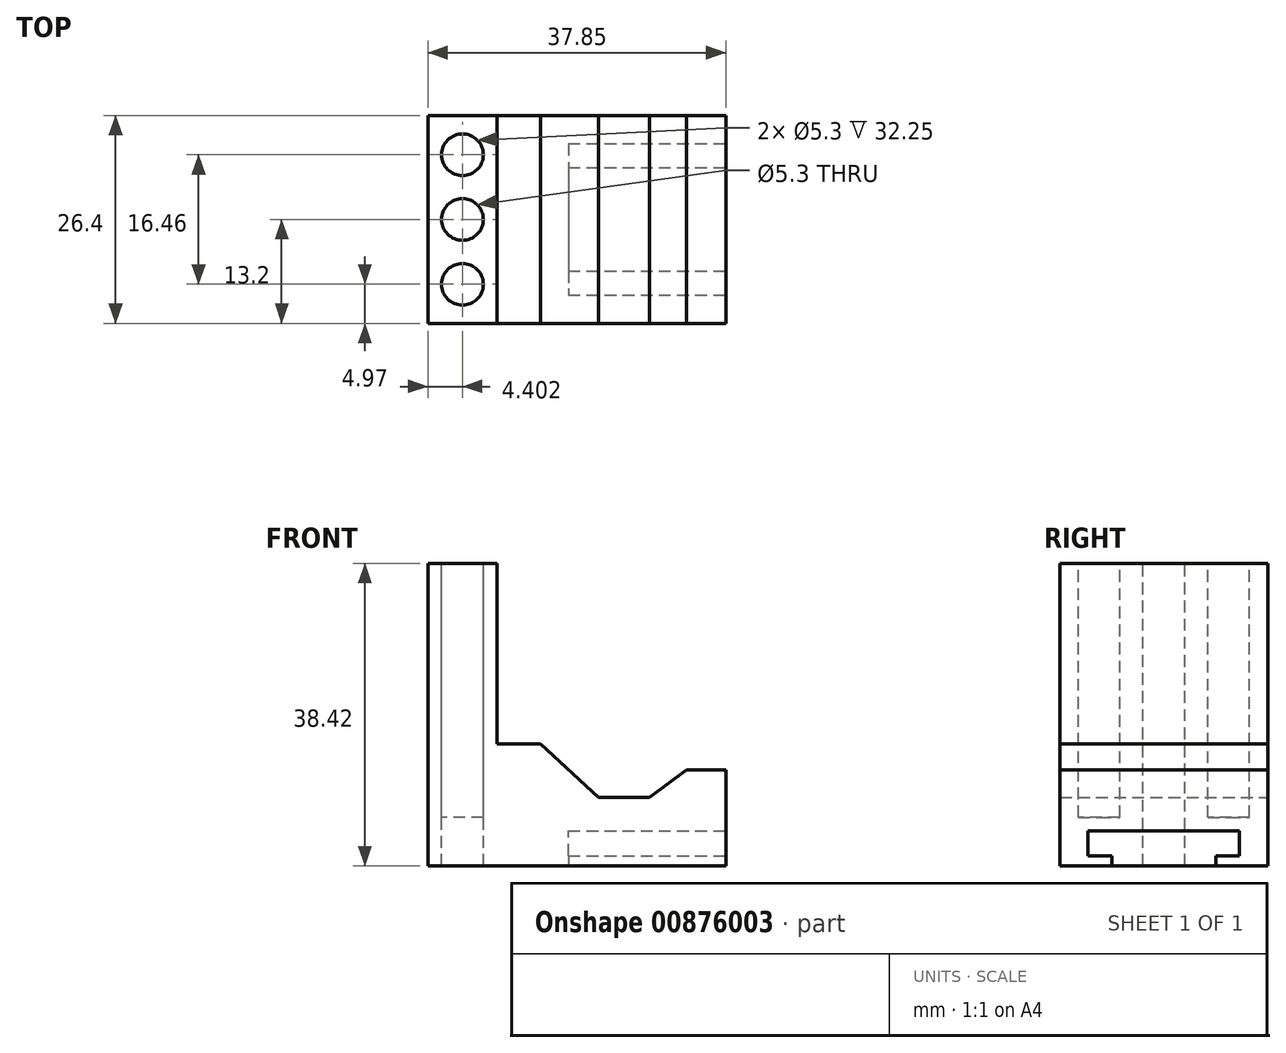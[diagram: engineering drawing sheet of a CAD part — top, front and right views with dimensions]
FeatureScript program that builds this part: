
annotation { "Feature Type Name" : "Feature", "Feature Type Description" : "" }
export const myFeature = defineFeature(function(context is Context, id is Id, definition is map)
    precondition{}
    {
        {
            var Q0;
            Q0=qCreatedBy(makeId("Front.planeOp"),FACE);
            var sketch = newSketch(context, id + "F0", { "sketchPlane" : qUnion([Q0])});
            skLineSegment(sketch, "E0", {"start": v(-21.52, 22.9) * mm, "end": v(-21.52, -15.51) * mm});
            skLineSegment(sketch, "E1", {"start": v(-21.52, -15.51) * mm, "end": v(16.33, -15.51) * mm});
            skLineSegment(sketch, "E2", {"start": v(16.33, -15.51) * mm, "end": v(16.33, -3.3) * mm});
            skLineSegment(sketch, "E3", {"start": v(16.33, -3.3) * mm, "end": v(11.33, -3.3) * mm});
            skLineSegment(sketch, "E4", {"start": v(11.33, -3.3) * mm, "end": v(6.63, -6.78) * mm});
            skLineSegment(sketch, "E5", {"start": v(6.63, -6.78) * mm, "end": v(0.13, -6.78) * mm});
            skLineSegment(sketch, "E6", {"start": v(0.13, -6.78) * mm, "end": v(-7.22, 0) * mm});
            skLineSegment(sketch, "E7", {"start": v(-7.22, 0) * mm, "end": v(-12.72, 0) * mm});
            skLineSegment(sketch, "E8", {"start": v(-12.72, 0) * mm, "end": v(-12.72, 22.9) * mm});
            skLineSegment(sketch, "E9", {"start": v(-12.72, 22.9) * mm, "end": v(-21.52, 22.9) * mm});
            skSolve(sketch);
        }
        {
            var Q0;
            Q0=makeQuery(id+"F0.imprint","IMPRINT",FACE,{"disambiguationData":[TD([[makeQuery(id+"F0.imprint","IMPRINT",EDGE,{"derivedFrom":sQuery(id+"F0.wireOp",EDGE,"E0")}),1.0]])]});
            extrude(context, id + "F1", {"entities" : qUnion([Q0]), "depth" : 26.4 * mm, "offsetDistance" : 25 * mm});
        }
        {
            var Q0;
            Q0=makeQuery(id+"F1.opExtrude","SWEPT_FACE",FACE,{"disambiguationData":[OSD([sQuery(id+"F0.wireOp",EDGE,"E9")])]});
            var sketch = newSketch(context, id + "F2", { "sketchPlane" : qUnion([Q0])});
            skLineSegment(sketch, "E10", {"start": v(-17.12, 0) * mm, "end": v(-17.12, -26.4) * mm, "construction": true});
            skLineSegment(sketch, "E11", {"start": v(-21.52, -13.2) * mm, "end": v(-12.72, -13.2) * mm, "construction": true});
            skCircle(sketch, "E12", {"center": v(-17.12, -13.2) * mm, "radius": 2.65 * mm});
            skCircle(sketch, "E13", {"center": v(-17.12, -21.43) * mm, "radius": 2.65 * mm});
            skCircle(sketch, "E14", {"center": v(-17.12, -4.97) * mm, "radius": 2.65 * mm});
            skSolve(sketch);
        }
        {
            var Q0;
            Q0=makeQuery(id+"F2.imprint","IMPRINT",FACE,{"disambiguationData":[TD([[makeQuery(id+"F2.imprint","IMPRINT",EDGE,{"derivedFrom":sQuery(id+"F2.wireOp",EDGE,"E14")}),1.0]])]});
            var Q1;
            Q1=makeQuery(id+"F2.imprint","IMPRINT",FACE,{"disambiguationData":[TD([[makeQuery(id+"F2.imprint","IMPRINT",EDGE,{"derivedFrom":sQuery(id+"F2.wireOp",EDGE,"E13")}),1.0]])]});
            extrude(context, id + "F3", {"entities" : qUnion([Q0, Q1]), "operationType" : NewBodyOperationType.REMOVE, "oppositeDirection" : true, "depth" : 32.25 * mm, "offsetDistance" : 25 * mm});
        }
        {
            var Q0;
            Q0=makeQuery(id+"F2.imprint","IMPRINT",FACE,{"disambiguationData":[TD([[makeQuery(id+"F2.imprint","IMPRINT",EDGE,{"derivedFrom":sQuery(id+"F2.wireOp",EDGE,"E12")}),1.0]])]});
            extrude(context, id + "F4", {"entities" : qUnion([Q0]), "operationType" : NewBodyOperationType.REMOVE, "oppositeDirection" : true, "depth" : 40 * mm, "offsetDistance" : 25 * mm});
        }
        {
            var Q0;
            Q0=makeQuery(id+"F1.opExtrude","SWEPT_FACE",FACE,{"disambiguationData":[OSD([sQuery(id+"F0.wireOp",EDGE,"E1")])]});
            var sketch = newSketch(context, id + "F5", { "sketchPlane" : qUnion([Q0])});
            skLineSegment(sketch, "E15", {"start": v(-21.52, 13.2) * mm, "end": v(16.33, 13.2) * mm, "construction": true});
            skLineSegment(sketch, "E16", {"start": v(-3.67, 6.62) * mm, "end": v(-3.67, 19.78) * mm});
            skLineSegment(sketch, "E17", {"start": v(-3.67, 19.78) * mm, "end": v(16.33, 19.78) * mm});
            skLineSegment(sketch, "E18", {"start": v(-3.67, 6.62) * mm, "end": v(16.33, 6.62) * mm});
            skSolve(sketch);
        }
        {
            var Q0;
            Q0=makeQuery(id+"F5.imprint","IMPRINT",FACE,{"disambiguationData":[TD([[makeQuery(id+"F5.imprint","IMPRINT",EDGE,{"derivedFrom":sQuery(id+"F5.wireOp",EDGE,"E16")}),-1.0]])]});
            extrude(context, id + "F6", {"entities" : qUnion([Q0]), "operationType" : NewBodyOperationType.REMOVE, "oppositeDirection" : true, "depth" : 4.45 * mm, "offsetDistance" : 25 * mm});
        }
        {
            var Q0;
            Q0=makeQuery(id+"F1.opExtrude","SWEPT_FACE",FACE,{"disambiguationData":[OSD([sQuery(id+"F0.wireOp",EDGE,"E2")])]});
            var sketch = newSketch(context, id + "F7", { "sketchPlane" : qUnion([Q0])});
            skLineSegment(sketch, "E19.bottom", {"start": v(-3.57, -14.21) * mm, "end": v(-22.82, -14.21) * mm});
            skLineSegment(sketch, "E19.top", {"start": v(-3.57, -11.06) * mm, "end": v(-22.82, -11.06) * mm});
            skLineSegment(sketch, "E19.left", {"start": v(-3.57, -14.21) * mm, "end": v(-3.57, -11.06) * mm});
            skLineSegment(sketch, "E19.right", {"start": v(-22.82, -14.21) * mm, "end": v(-22.82, -11.06) * mm});
            skPoint(sketch, "E19.middle", {"position": v(-13.2, -12.64) * mm});
            skSolve(sketch);
        }
        {
            var Q0;
            {var subQ0=sQuery(id+"F7.wireOp",EDGE,"E19.bottom");var subQ1=sQuery(id+"F0.wireOp",EDGE,"E2");var subQ2=sQuery(id+"F0.wireOp",EDGE,"E1");var subQ3=makeQuery(id+"F6.boolean.opBoolean","COPY",EDGE,{"derivedFrom":makeQuery(id+"F6.opExtrude","SWEPT_EDGE",EDGE,{"disambiguationData":[OSD([subQ2,subQ1,sQuery(id+"F5.wireOp",EDGE,"E18")])]})});var subQ4=makeQuery(id+"F7.imprint","INTERSECT",VERTEX,{"derivedFrom":[subQ3,subQ0]});Q0=makeQuery(id+"F7.imprint","IMPRINT",FACE,{"disambiguationData":[TD([[makeQuery(id+"F7.imprint","IMPRINT",EDGE,{"disambiguationData":[TD([[subQ4,-1.0]])],"derivedFrom":subQ0}),-1.0]])]});}
            var Q1;
            {var subQ0=sQuery(id+"F7.wireOp",EDGE,"E19.left");Q1=makeQuery(id+"F7.imprint","IMPRINT",FACE,{"disambiguationData":[TD([[makeQuery(id+"F7.imprint","IMPRINT",EDGE,{"derivedFrom":subQ0}),1.0]])]});}
            var Q2;
            {var subQ0=sQuery(id+"F7.wireOp",EDGE,"E19.right");Q2=makeQuery(id+"F7.imprint","IMPRINT",FACE,{"disambiguationData":[TD([[makeQuery(id+"F7.imprint","IMPRINT",EDGE,{"derivedFrom":subQ0}),-1.0]])]});}
            extrude(context, id + "F8", {"entities" : qUnion([Q0, Q1, Q2]), "operationType" : NewBodyOperationType.REMOVE, "oppositeDirection" : true, "depth" : 20 * mm, "offsetDistance" : 25 * mm});
        }
    });
